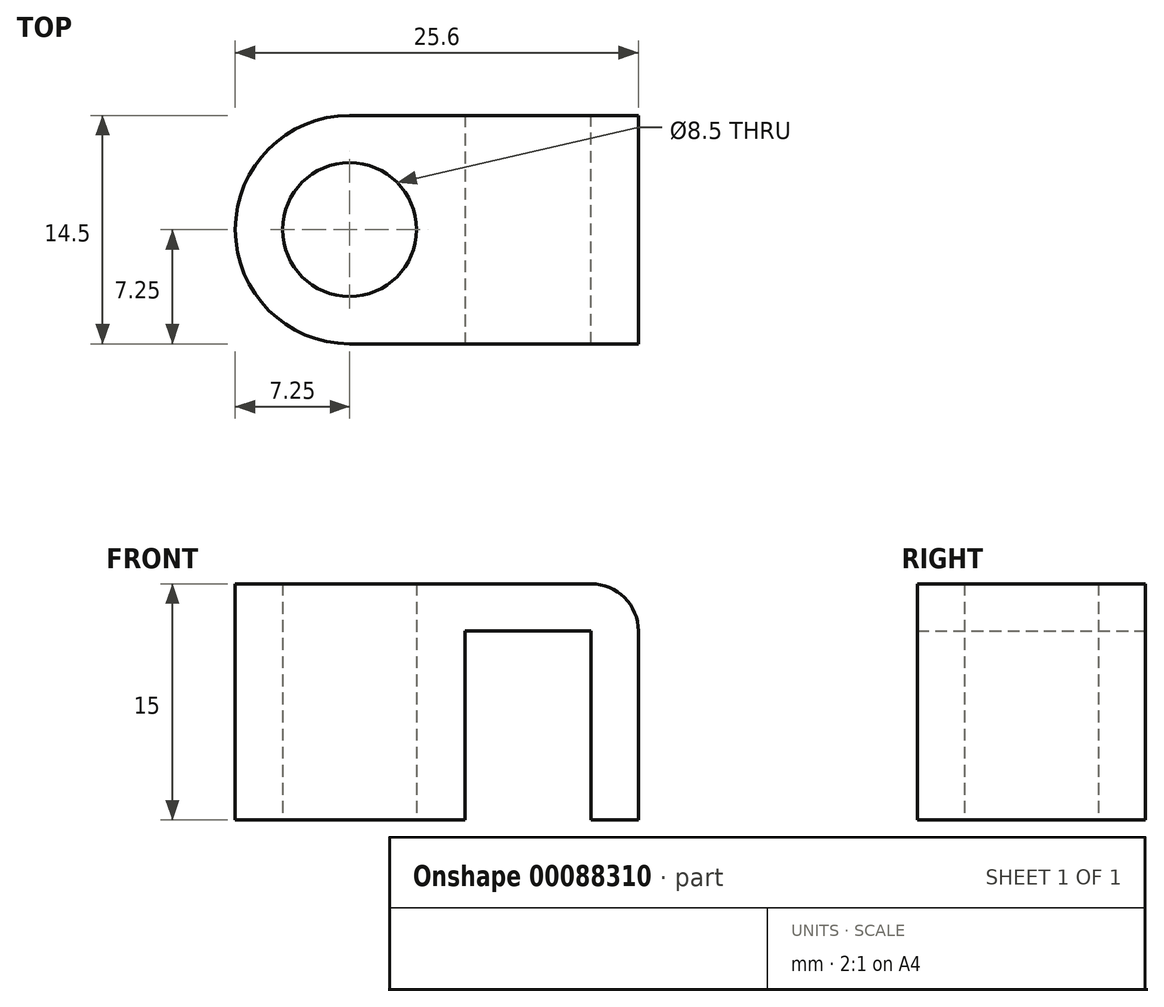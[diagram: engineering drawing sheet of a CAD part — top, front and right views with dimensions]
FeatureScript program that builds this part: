
annotation { "Feature Type Name" : "Feature", "Feature Type Description" : "" }
export const myFeature = defineFeature(function(context is Context, id is Id, definition is map)
    precondition{}
    {
        {
            var Q0;
            Q0=qCreatedBy(makeId("Top.planeOp"),FACE);
            var sketch = newSketch(context, id + "F0", { "sketchPlane" : qUnion([Q0])});
            skCircle(sketch, "E0", {"center": v(0, 0) * mm, "radius": 4.25 * mm});
            skCircle(sketch, "E1", {"center": v(0, 0) * mm, "radius": 7.25 * mm});
            skLineSegment(sketch, "E2", {"start": v(0, 7.25) * mm, "end": v(18.35, 7.25) * mm});
            skLineSegment(sketch, "E3", {"start": v(18.35, 7.25) * mm, "end": v(18.35, -7.25) * mm});
            skLineSegment(sketch, "E4", {"start": v(0, -7.25) * mm, "end": v(18.35, -7.25) * mm});
            skLineSegment(sketch, "E5", {"start": v(7.25, 0) * mm, "end": v(7.25, 7.25) * mm});
            skLineSegment(sketch, "E6", {"start": v(7.25, 0) * mm, "end": v(7.25, -7.25) * mm});
            skLineSegment(sketch, "E7", {"start": v(7.35, 7.25) * mm, "end": v(7.35, -7.25) * mm, "construction": true});
            skLineSegment(sketch, "E8", {"start": v(15.35, 7.25) * mm, "end": v(15.35, -7.25) * mm, "construction": true});
            skLineSegment(sketch, "E9", {"start": v(7.35, 7.25) * mm, "end": v(7.35, -7.25) * mm});
            skLineSegment(sketch, "E10", {"start": v(15.35, -7.25) * mm, "end": v(15.35, 7.25) * mm});
            skSolve(sketch);
        }
        {
            var Q0;
            Q0=qSketchRegion(id+"F0",true);
            extrude(context, id + "F1", {"entities" : qUnion([Q0]), "depth" : 3 * mm});
        }
        {
            var Q0;
            Q0=makeQuery(id+"F0.imprint","IMPRINT",FACE,{"disambiguationData":[TD([[makeQuery(id+"F0.imprint","IMPRINT",EDGE,{"derivedFrom":sQuery(id+"F0.wireOp",EDGE,"E0")}),-1.0]])]});
            var Q1;
            {var subQ3=sQuery(id+"F0.wireOp",EDGE,"E5");Q1=makeQuery(id+"F0.imprint","IMPRINT",FACE,{"disambiguationData":[TD([[makeQuery(id+"F0.imprint","IMPRINT",EDGE,{"derivedFrom":subQ3}),1.0]])]});}
            var Q2;
            {var subQ1=sQuery(id+"F0.wireOp",EDGE,"E5");Q2=makeQuery(id+"F0.imprint","IMPRINT",FACE,{"disambiguationData":[TD([[makeQuery(id+"F0.imprint","IMPRINT",EDGE,{"derivedFrom":subQ1}),-1.0]])]});}
            var Q3;
            {var subQ0=sQuery(id+"F0.wireOp",EDGE,"E3");Q3=makeQuery(id+"F0.imprint","IMPRINT",FACE,{"disambiguationData":[TD([[makeQuery(id+"F0.imprint","IMPRINT",EDGE,{"derivedFrom":subQ0}),-1.0]])]});}
            var Q4;
            {var subQ3=sQuery(id+"F0.wireOp",EDGE,"E6");Q4=makeQuery(id+"F0.imprint","IMPRINT",FACE,{"disambiguationData":[TD([[makeQuery(id+"F0.imprint","IMPRINT",EDGE,{"derivedFrom":subQ3}),-1.0]])]});}
            extrude(context, id + "F2", {"entities" : qUnion([Q0, Q1, Q2, Q3, Q4]), "operationType" : NewBodyOperationType.ADD, "oppositeDirection" : true, "depth" : 12 * mm, "offsetDistance" : 25 * mm});
        }
        {
            var Q0;
            Q0=makeQuery(id+"F2.opExtrude","CAP_EDGE",EDGE,{"disambiguationData":[OSD([sQuery(id+"F0.wireOp",EDGE,"E9")])],"isStart":true});
            var Q1;
            Q1=makeQuery(id+"F2.opExtrude","CAP_EDGE",EDGE,{"disambiguationData":[OSD([sQuery(id+"F0.wireOp",EDGE,"E10")])],"isStart":true});
            var Q2;
            Q2=makeQuery(id+"F1.opExtrude","CAP_EDGE",EDGE,{"disambiguationData":[OSD([sQuery(id+"F0.wireOp",EDGE,"E3")])],"isStart":false});
            fillet(context, id + "F3", {"entities" : qUnion([Q0, Q1, Q2]), "radius" : 3 * mm, "tangentPropagation" : true, "allowEdgeOverflow" : false});
        }
        {
            var Q0;
            Q0=makeQuery(id+"F2.opExtrude","CAP_FACE",FACE,{"disambiguationData":[OSD([sQuery(id+"F0.wireOp",EDGE,"E0"),sQuery(id+"F0.wireOp",EDGE,"E1"),sQuery(id+"F0.wireOp",EDGE,"E2"),sQuery(id+"F0.wireOp",EDGE,"E4"),sQuery(id+"F0.wireOp",EDGE,"E9")])],"isStart":false});
            cPlane(context, id + "F4", {"entities" : qUnion([Q0]), "cplaneType" : CPlaneType.OFFSET, "offset" : 25 * mm, "width" : 150 * mm, "height" : 150 * mm});
        }
        {
            var Q0;
            Q0=qCreatedBy(id+"F4.planeOp",FACE);
            var sketch = newSketch(context, id + "F5", { "sketchPlane" : qUnion([Q0])});
            skCircle(sketch, "E11.0", {"center": v(0, 0) * mm, "radius": 4.25 * mm});
            skArc(sketch, "E12.0.0", {"start": v(0, 7.25) * mm, "mid": v(-7.25, 0) * mm, "end": v(0, -7.25) * mm});
            skLineSegment(sketch, "E12.0.1", {"start": v(0, -7.25) * mm, "end": v(7.35, -7.25) * mm});
            skLineSegment(sketch, "E12.0.2", {"start": v(7.35, -7.25) * mm, "end": v(7.35, 7.25) * mm});
            skLineSegment(sketch, "E12.0.3", {"start": v(7.35, 7.25) * mm, "end": v(0, 7.25) * mm});
            skLineSegment(sketch, "E13", {"start": v(0, -7.25) * mm, "end": v(-37.25, -7.25) * mm});
            skLineSegment(sketch, "E14", {"start": v(-37.25, -7.25) * mm, "end": v(-37.25, -4) * mm});
            skLineSegment(sketch, "E15", {"start": v(-37.25, 7.25) * mm, "end": v(0, 7.25) * mm});
            skLineSegment(sketch, "E16.bottom", {"start": v(0, 0) * mm, "end": v(-22.25, 0) * mm, "construction": true});
            skLineSegment(sketch, "E16.top", {"start": v(0, 4) * mm, "end": v(-37.25, 4) * mm, "construction": true});
            skLineSegment(sketch, "E16.left", {"start": v(0, 0) * mm, "end": v(0, 4) * mm, "construction": true});
            skLineSegment(sketch, "E17.MirrorCS", {"start": v(0, -4) * mm, "end": v(-37.25, -4) * mm, "construction": true});
            skLineSegment(sketch, "E18", {"start": v(-37.25, 0) * mm, "end": v(-7.25, 0) * mm, "construction": true});
            skPoint(sketch, "E19", {"position": v(-22.25, 0) * mm});
            skArc(sketch, "E20", {"start": v(-22.25, -4) * mm, "mid": v(-18.25, 0) * mm, "end": v(-22.25, 4) * mm});
            skLineSegment(sketch, "E21", {"start": v(-22.25, 4) * mm, "end": v(-37.25, 4) * mm});
            skLineSegment(sketch, "E22", {"start": v(-37.25, -4) * mm, "end": v(-22.25, -4) * mm});
            skLineSegment(sketch, "E23.trimOffspring", {"start": v(-37.25, 4) * mm, "end": v(-37.25, 7.25) * mm});
            skSolve(sketch);
        }
        {
            var Q0;
            Q0=makeQuery(id+"F5.imprint","IMPRINT",FACE,{"disambiguationData":[TD([[makeQuery(id+"F5.imprint","IMPRINT",EDGE,{"derivedFrom":sQuery(id+"F5.wireOp",EDGE,"E11.0")}),-1.0]])]});
            extrude(context, id + "F6", {"entities" : qUnion([Q0]), "oppositeDirection" : true, "depth" : 22 * mm});
        }
        {
            var Q0;
            Q0=qSketchRegion(id+"F5",true);
            extrude(context, id + "F7", {"entities" : qUnion([Q0]), "operationType" : NewBodyOperationType.ADD, "depth" : 3 * mm});
        }
        {
            var Q0;
            Q0=makeQuery(id+"F7.opExtrude","SWEPT_EDGE",EDGE,{"disambiguationData":[OSD([sQuery(id+"F5.wireOp",EDGE,"E15"),sQuery(id+"F5.wireOp",EDGE,"E23.trimOffspring")])]});
            var Q1;
            Q1=makeQuery(id+"F7.opExtrude","SWEPT_EDGE",EDGE,{"disambiguationData":[OSD([sQuery(id+"F5.wireOp",EDGE,"E13"),sQuery(id+"F5.wireOp",EDGE,"E14")])]});
            fillet(context, id + "F8", {"entities" : qUnion([Q0, Q1]), "radius" : 5 * mm, "tangentPropagation" : true, "allowEdgeOverflow" : false});
        }
        {
            var Q0;
            Q0=makeQuery(id+"F6.opExtrude","SWEPT_BODY",BODY,{"disambiguationData":[OSD([sQuery(id+"F5.wireOp",EDGE,"E11.0"),sQuery(id+"F5.wireOp",EDGE,"E12.0.0"),sQuery(id+"F5.wireOp",EDGE,"E12.0.1"),sQuery(id+"F5.wireOp",EDGE,"E12.0.2"),sQuery(id+"F5.wireOp",EDGE,"E12.0.3")])]});
            deleteBodies(context, id + "F9", {"entities" : qUnion([Q0])});
        }
    });
